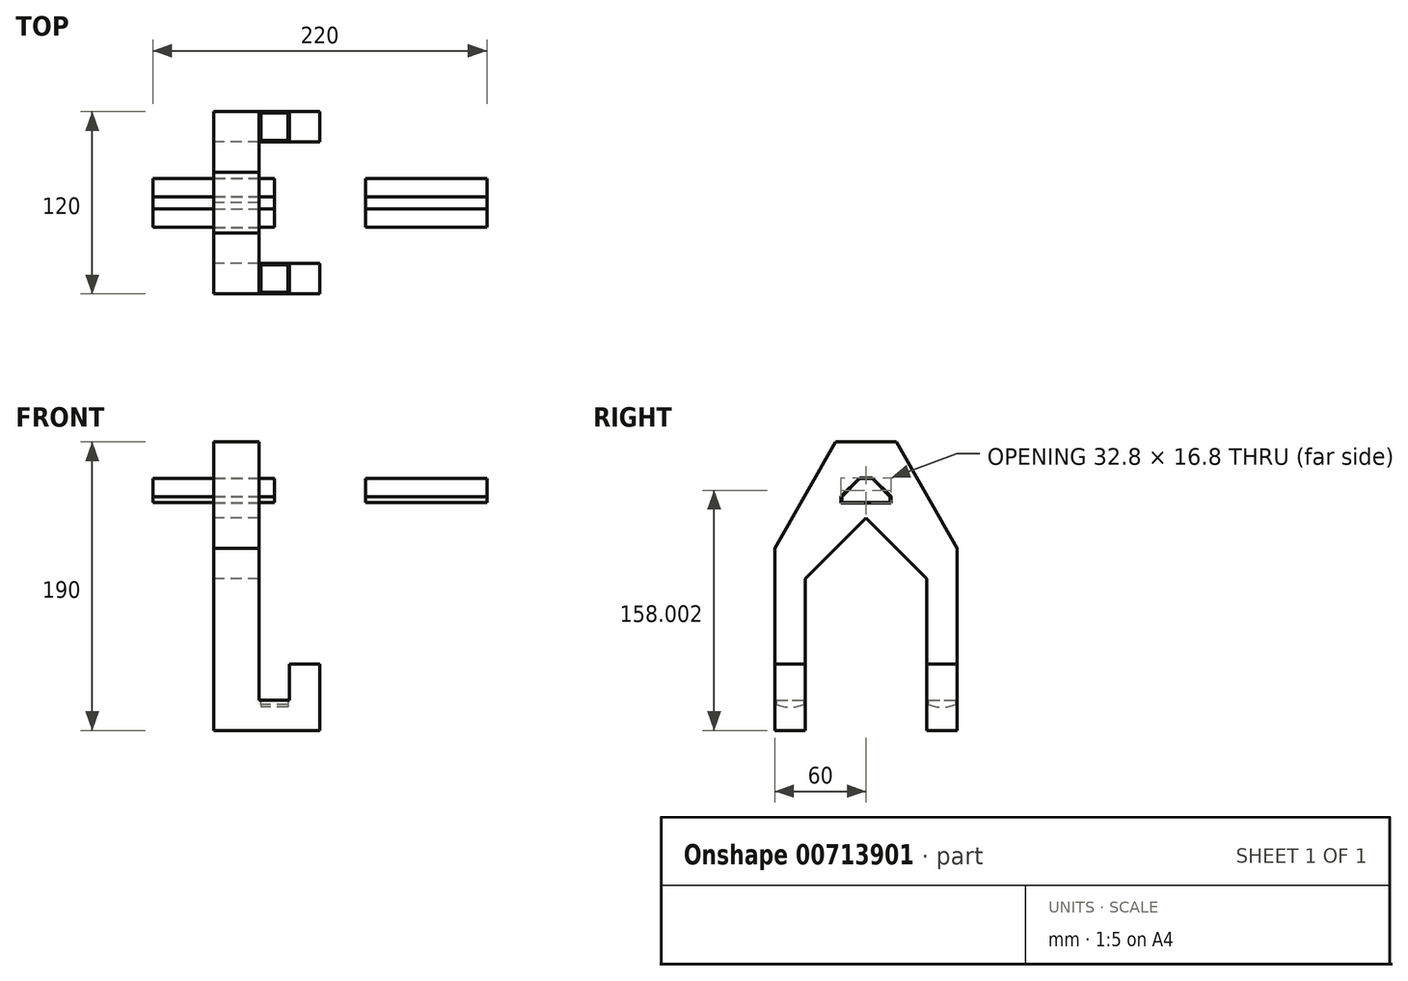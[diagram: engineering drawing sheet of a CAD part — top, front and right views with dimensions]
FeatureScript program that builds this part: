
annotation { "Feature Type Name" : "Feature", "Feature Type Description" : "" }
export const myFeature = defineFeature(function(context is Context, id is Id, definition is map)
    precondition{}
    {
        {
            var Q0;
            Q0=qCreatedBy(makeId("Front.planeOp"),FACE);
            var sketch = newSketch(context, id + "F0", { "sketchPlane" : qUnion([Q0])});
            skLineSegment(sketch, "E0", {"start": v(0, -71.5) * mm, "end": v(70, -71.5) * mm});
            skLineSegment(sketch, "E1", {"start": v(70, -71.5) * mm, "end": v(70, -27.82) * mm});
            skLineSegment(sketch, "E2", {"start": v(70, -27.82) * mm, "end": v(50, -27.82) * mm});
            skLineSegment(sketch, "E3", {"start": v(50, -27.82) * mm, "end": v(50, -51.5) * mm});
            skLineSegment(sketch, "E4", {"start": v(50, -51.5) * mm, "end": v(30, -51.5) * mm});
            skLineSegment(sketch, "E5", {"start": v(30, -51.5) * mm, "end": v(30, 0) * mm});
            skLineSegment(sketch, "E6", {"start": v(30, 0) * mm, "end": v(30, 118.5) * mm});
            skLineSegment(sketch, "E7", {"start": v(30, 118.5) * mm, "end": v(0, 118.5) * mm});
            skLineSegment(sketch, "E8", {"start": v(0, 118.5) * mm, "end": v(0, -71.5) * mm});
            skLineSegment(sketch, "E9", {"start": v(49, -51.5) * mm, "end": v(49, -54.5) * mm});
            skLineSegment(sketch, "E10", {"start": v(49, -54.5) * mm, "end": v(31, -54.5) * mm});
            skLineSegment(sketch, "E11", {"start": v(31, -54.5) * mm, "end": v(31, -51.5) * mm});
            skSolve(sketch);
        }
        {
            var Q0;
            Q0=makeQuery(id+"F0.imprint","IMPRINT",FACE,{"disambiguationData":[TD([[makeQuery(id+"F0.imprint","IMPRINT",EDGE,{"derivedFrom":sQuery(id+"F0.wireOp",EDGE,"E0")}),1.0]])]});
            var Q1;
            {var subQ0=sQuery(id+"F0.wireOp",EDGE,"E9");Q1=makeQuery(id+"F0.imprint","IMPRINT",FACE,{"disambiguationData":[TD([[makeQuery(id+"F0.imprint","IMPRINT",EDGE,{"derivedFrom":subQ0}),-1.0]])]});}
            extrude(context, id + "F1", {"entities" : qUnion([Q0, Q1]), "endBound" : BoundingType.SYMMETRIC, "depth" : 120 * mm, "offsetDistance" : 25 * mm, "hasSecondDirection" : true, "secondDirectionOppositeDirection" : true, "secondDirectionDepth" : 25 * mm});
        }
        {
            var Q0;
            Q0=makeQuery(id+"F1.opExtrude","SWEPT_FACE",FACE,{"disambiguationData":[OSD([sQuery(id+"F0.wireOp",EDGE,"E8")])]});
            var sketch = newSketch(context, id + "F2", { "sketchPlane" : qUnion([Q0])});
            skLineSegment(sketch, "E12.bottom", {"start": v(-40, -71.5) * mm, "end": v(40, -71.5) * mm});
            skLineSegment(sketch, "E12.top", {"start": v(-40, 28.5) * mm, "end": v(40, 28.5) * mm});
            skLineSegment(sketch, "E12.left", {"start": v(-40, -71.5) * mm, "end": v(-40, 28.5) * mm});
            skLineSegment(sketch, "E12.right", {"start": v(40, -71.5) * mm, "end": v(40, 28.5) * mm});
            skLineSegment(sketch, "E13", {"start": v(-40, 28.5) * mm, "end": v(0, 68.5) * mm});
            skLineSegment(sketch, "E14", {"start": v(0, 68.5) * mm, "end": v(40, 28.5) * mm});
            skSolve(sketch);
        }
        {
            var Q0;
            Q0=makeQuery(id+"F2.imprint","IMPRINT",FACE,{"disambiguationData":[TD([[makeQuery(id+"F2.imprint","IMPRINT",EDGE,{"derivedFrom":sQuery(id+"F2.wireOp",EDGE,"E12.bottom")}),-1.0]])]});
            var Q1;
            Q1=makeQuery(id+"F2.imprint","IMPRINT",FACE,{"disambiguationData":[TD([[makeQuery(id+"F2.imprint","IMPRINT",EDGE,{"derivedFrom":sQuery(id+"F2.wireOp",EDGE,"E12.top")}),1.0]])]});
            extrude(context, id + "F3", {"entities" : qUnion([Q0, Q1]), "operationType" : NewBodyOperationType.REMOVE, "endBound" : BoundingType.THROUGH_ALL, "oppositeDirection" : true, "depth" : 25 * mm, "offsetDistance" : 25 * mm});
        }
        {
            var Q0;
            Q0=makeQuery(id+"F1.opExtrude","SWEPT_FACE",FACE,{"disambiguationData":[OSD([sQuery(id+"F0.wireOp",EDGE,"E8")])]});
            var sketch = newSketch(context, id + "F4", { "sketchPlane" : qUnion([Q0])});
            skLineSegment(sketch, "E15", {"start": v(-60, 118.5) * mm, "end": v(-108, 118.5) * mm});
            skLineSegment(sketch, "E16", {"start": v(-108, 118.5) * mm, "end": v(-108, 68.5) * mm});
            skLineSegment(sketch, "E17", {"start": v(-108, 68.5) * mm, "end": v(-88, 68.5) * mm});
            skLineSegment(sketch, "E18", {"start": v(-88, 68.5) * mm, "end": v(-88, 96.5) * mm});
            skLineSegment(sketch, "E19", {"start": v(-86, 98.5) * mm, "end": v(-62, 98.5) * mm});
            skPoint(sketch, "E20", {"position": v(-84.6, 98.5) * mm});
            skPoint(sketch, "E21", {"position": v(-62.05, 98.5) * mm});
            skPoint(sketch, "E22.visualSharp", {"position": v(-88, 98.5) * mm});
            skArc(sketch, "E22.filletArc", {"start": v(-86, 98.5) * mm, "mid": v(-87.41, 97.9) * mm, "end": v(-88, 96.5) * mm});
            skLineSegment(sketch, "E23", {"start": v(-60, 96.5) * mm, "end": v(-60, 92.19) * mm});
            skPoint(sketch, "E24.visualSharp", {"position": v(-60, 98.5) * mm});
            skArc(sketch, "E24.filletArc", {"start": v(-60, 96.5) * mm, "mid": v(-60.59, 97.9) * mm, "end": v(-62, 98.5) * mm});
            skLineSegment(sketch, "E25", {"start": v(-60, 98.5) * mm, "end": v(-60, 13.5) * mm});
            skLineSegment(sketch, "E26", {"start": v(-60, 13.5) * mm, "end": v(-108.1, 13.5) * mm});
            skLineSegment(sketch, "E27", {"start": v(-108.1, 13.5) * mm, "end": v(-60, -34.62) * mm});
            skLineSegment(sketch, "E28", {"start": v(-60, 13.5) * mm, "end": v(-60, -34.62) * mm});
            skSolve(sketch);
        }
        {
            var Q0;
            {var subQ0=sQuery(id+"F0.wireOp",EDGE,"E8");Q0=makeQuery(id+"FtPaMowYWSEWgdu_1.boolean.opBoolean","MERGE",FACE,{"derivedFrom":[makeQuery(id+"F1.opExtrude","SWEPT_FACE",FACE,{"disambiguationData":[OSD([subQ0])]}),makeQuery(id+"FtPaMowYWSEWgdu_1.opExtrude","CAP_FACE",FACE,{"disambiguationData":[OSD([subQ0,sQuery(id+"F4.wireOp",EDGE,"E15"),sQuery(id+"F4.wireOp",EDGE,"E16"),sQuery(id+"F4.wireOp",EDGE,"E17"),sQuery(id+"F4.wireOp",EDGE,"E18"),sQuery(id+"F4.wireOp",EDGE,"E19"),sQuery(id+"F4.wireOp",EDGE,"E22.filletArc"),sQuery(id+"F4.wireOp",EDGE,"E24.filletArc")])],"isStart":true})]});}
            var sketch = newSketch(context, id + "F5", { "sketchPlane" : qUnion([Q0])});
            skLineSegment(sketch, "E29", {"start": v(-42.74, 118.5) * mm, "end": v(60, 118.5) * mm});
            skLineSegment(sketch, "E30", {"start": v(60, 118.5) * mm, "end": v(60, 41.85) * mm});
            skLineSegment(sketch, "E31", {"start": v(-40, 28.5) * mm, "end": v(40, 28.5) * mm});
            skLineSegment(sketch, "E32", {"start": v(-40, 118.5) * mm, "end": v(-40, 98.5) * mm});
            skLineSegment(sketch, "E33", {"start": v(-40, 98.5) * mm, "end": v(0, 98.5) * mm});
            skLineSegment(sketch, "E34", {"start": v(0, 98.5) * mm, "end": v(0, 78.5) * mm});
            skLineSegment(sketch, "E35", {"start": v(0, 78.5) * mm, "end": v(20, 78.5) * mm});
            skLineSegment(sketch, "E36", {"start": v(20, 78.5) * mm, "end": v(0, 98.5) * mm});
            skLineSegment(sketch, "E37", {"start": v(0, 98.5) * mm, "end": v(-20, 78.5) * mm});
            skLineSegment(sketch, "E38", {"start": v(-20, 78.5) * mm, "end": v(0, 78.5) * mm});
            skLineSegment(sketch, "E39", {"start": v(-20, 78.5) * mm, "end": v(-20, 118.5) * mm});
            skLineSegment(sketch, "E40", {"start": v(-20, 118.5) * mm, "end": v(-60, 48.5) * mm});
            skLineSegment(sketch, "E41", {"start": v(-60, 48.5) * mm, "end": v(-60, 28.5) * mm});
            skLineSegment(sketch, "E42", {"start": v(-60, 28.5) * mm, "end": v(-40, 28.5) * mm});
            skLineSegment(sketch, "E43", {"start": v(40, 28.5) * mm, "end": v(60, 28.5) * mm});
            skLineSegment(sketch, "E44", {"start": v(60, 28.5) * mm, "end": v(60, 48.5) * mm});
            skLineSegment(sketch, "E45", {"start": v(60, 48.5) * mm, "end": v(20, 118.5) * mm});
            skLineSegment(sketch, "E46", {"start": v(16, 82.5) * mm, "end": v(16, 78.5) * mm});
            skLineSegment(sketch, "E47", {"start": v(-16, 82.5) * mm, "end": v(-16, 78.5) * mm});
            skLineSegment(sketch, "E48", {"start": v(4, 94.5) * mm, "end": v(-4, 94.5) * mm});
            skSolve(sketch);
        }
        {
            var Q0;
            {var subQ0=sQuery(id+"F0.wireOp",EDGE,"E9");Q0=makeQuery(id+"F0.imprint","IMPRINT",FACE,{"disambiguationData":[TD([[makeQuery(id+"F0.imprint","IMPRINT",EDGE,{"derivedFrom":subQ0}),-1.0]])]});}
            extrude(context, id + "F6", {"entities" : qUnion([Q0]), "depth" : 18 * mm, "offsetDistance" : 25 * mm});
        }
        {
            var Q0;
            Q0=makeQuery(id+"F6.opExtrude","SWEPT_FACE",FACE,{"disambiguationData":[OSD([sQuery(id+"F0.wireOp",EDGE,"E11")])]});
            var sketch = newSketch(context, id + "F7", { "sketchPlane" : qUnion([Q0])});
            skArc(sketch, "E49", {"start": v(0, -54.5) * mm, "mid": v(9, -56.2) * mm, "end": v(18, -54.5) * mm});
            skSolve(sketch);
        }
        {
            var Q0;
            Q0 = qSketchRegion(id + "F7", true);
            var Q1;
            Q1=makeQuery(id+"F7.imprint","IMPRINT",FACE,{"disambiguationData":[TD([[makeQuery(id+"F7.imprint","IMPRINT",EDGE,{"derivedFrom":sQuery(id+"F7.wireOp",EDGE,"E49")}),1.0]])]});
            var Q2;
            Q2=makeQuery(id+"F6.opExtrude","CAP_VERTEX",VERTEX,{"disambiguationData":[OSD([sQuery(id+"F0.wireOp",EDGE,"E9"),sQuery(id+"F0.wireOp",EDGE,"E10")])],"isStart":false});
            extrude(context, id + "F8", {"entities" : qUnion([Q0, Q1]), "operationType" : NewBodyOperationType.ADD, "endBound" : BoundingType.UP_TO_VERTEX, "oppositeDirection" : true, "depth" : 25 * mm, "endBoundEntityVertex" : qUnion([Q2]), "offsetDistance" : 25 * mm});
        }
        {
            var Q0;
            Q0=makeQuery(id+"F6.opExtrude","SWEPT_BODY",BODY,{"disambiguationData":[OSD([sQuery(id+"F0.wireOp",EDGE,"E4"),sQuery(id+"F0.wireOp",EDGE,"E9"),sQuery(id+"F0.wireOp",EDGE,"E10"),sQuery(id+"F0.wireOp",EDGE,"E11")])]});
            transform(context, id + "F9", {"entities" : qUnion([Q0]), "transformType" : TransformType.TRANSLATION_3D, "dx" : 0 * mm, "dy" : -41 * mm, "dz" : 0 * mm, "makeCopy" : true});
        }
        {
            var Q0;
            Q0=makeQuery(id+"F6.opExtrude","SWEPT_BODY",BODY,{"disambiguationData":[OSD([sQuery(id+"F0.wireOp",EDGE,"E4"),sQuery(id+"F0.wireOp",EDGE,"E9"),sQuery(id+"F0.wireOp",EDGE,"E10"),sQuery(id+"F0.wireOp",EDGE,"E11")])]});
            transform(context, id + "F10", {"entities" : qUnion([Q0]), "transformType" : TransformType.TRANSLATION_3D, "dx" : 0 * mm, "dy" : 59 * mm, "dz" : 0 * mm, "makeCopy" : false});
        }
        {
            var Q0;
            Q0=makeQuery(id+"F9.opPattern","COPY",BODY,{"derivedFrom":makeQuery(id+"F6.opExtrude","SWEPT_BODY",BODY,{"disambiguationData":[OSD([sQuery(id+"F0.wireOp",EDGE,"E4"),sQuery(id+"F0.wireOp",EDGE,"E9"),sQuery(id+"F0.wireOp",EDGE,"E10"),sQuery(id+"F0.wireOp",EDGE,"E11")])]}),"instanceName":"1"});
            var Q1;
            Q1=makeQuery(id+"F6.opExtrude","SWEPT_BODY",BODY,{"disambiguationData":[OSD([sQuery(id+"F0.wireOp",EDGE,"E4"),sQuery(id+"F0.wireOp",EDGE,"E9"),sQuery(id+"F0.wireOp",EDGE,"E10"),sQuery(id+"F0.wireOp",EDGE,"E11")])]});
            var Q2;
            Q2=makeQuery(id+"F1.opExtrude","SWEPT_BODY",BODY,{"disambiguationData":[OSD([sQuery(id+"F0.wireOp",EDGE,"E0"),sQuery(id+"F0.wireOp",EDGE,"E1"),sQuery(id+"F0.wireOp",EDGE,"E2"),sQuery(id+"F0.wireOp",EDGE,"E3"),sQuery(id+"F0.wireOp",EDGE,"E4"),sQuery(id+"F0.wireOp",EDGE,"E5"),sQuery(id+"F0.wireOp",EDGE,"E6"),sQuery(id+"F0.wireOp",EDGE,"E7"),sQuery(id+"F0.wireOp",EDGE,"E8")])]});
            booleanBodies(context, id + "F11", {"operationType" : BooleanOperationType.SUBTRACTION, "tools" : qUnion([Q0, Q1]), "targets" : qUnion([Q2])});
        }
        {
            var Q0;
            {var subQ0=sQuery(id+"F5.wireOp",EDGE,"E47");Q0=makeQuery(id+"F5.imprint","IMPRINT",FACE,{"disambiguationData":[TD([[makeQuery(id+"F5.imprint","IMPRINT",EDGE,{"derivedFrom":subQ0}),1.0]])]});}
            var Q1;
            {var subQ0=sQuery(id+"F5.wireOp",EDGE,"E46");Q1=makeQuery(id+"F5.imprint","IMPRINT",FACE,{"disambiguationData":[TD([[makeQuery(id+"F5.imprint","IMPRINT",EDGE,{"derivedFrom":subQ0}),-1.0]])]});}
            extrude(context, id + "F12", {"entities" : qUnion([Q0, Q1]), "endBound" : BoundingType.SYMMETRIC, "depth" : 80 * mm, "offsetDistance" : 25 * mm});
        }
        {
            var Q0;
            {var subQ1=sQuery(id+"F5.wireOp",EDGE,"E32");Q0=makeQuery(id+"F5.imprint","IMPRINT",FACE,{"disambiguationData":[TD([[makeQuery(id+"F5.imprint","IMPRINT",EDGE,{"derivedFrom":subQ1}),-1.0]])]});}
            var Q1;
            {var subQ0=sQuery(id+"F5.wireOp",EDGE,"E32");Q1=makeQuery(id+"F5.imprint","IMPRINT",FACE,{"disambiguationData":[TD([[makeQuery(id+"F5.imprint","IMPRINT",EDGE,{"derivedFrom":subQ0}),1.0]])]});}
            var Q2;
            {var subQ0=sQuery(id+"F5.wireOp",EDGE,"E30");Q2=makeQuery(id+"F5.imprint","IMPRINT",FACE,{"disambiguationData":[TD([[makeQuery(id+"F5.imprint","IMPRINT",EDGE,{"derivedFrom":subQ0}),-1.0]])]});}
            extrude(context, id + "F13", {"entities" : qUnion([Q0, Q1, Q2]), "operationType" : NewBodyOperationType.REMOVE, "endBound" : BoundingType.THROUGH_ALL, "oppositeDirection" : true, "depth" : 25 * mm, "offsetDistance" : 25 * mm});
        }
        {
            var Q0;
            Q0=makeQuery(id+"F12.opExtrude","SWEPT_BODY",BODY,{"disambiguationData":[OSD([sQuery(id+"F5.wireOp",EDGE,"E35"),sQuery(id+"F5.wireOp",EDGE,"E36"),sQuery(id+"F5.wireOp",EDGE,"E37"),sQuery(id+"F5.wireOp",EDGE,"E38")])]});
            var Q1;
            Q1=makeQuery(id+"F1.opExtrude","SWEPT_BODY",BODY,{"disambiguationData":[OSD([sQuery(id+"F0.wireOp",EDGE,"E0"),sQuery(id+"F0.wireOp",EDGE,"E1"),sQuery(id+"F0.wireOp",EDGE,"E2"),sQuery(id+"F0.wireOp",EDGE,"E3"),sQuery(id+"F0.wireOp",EDGE,"E4"),sQuery(id+"F0.wireOp",EDGE,"E5"),sQuery(id+"F0.wireOp",EDGE,"E6"),sQuery(id+"F0.wireOp",EDGE,"E7"),sQuery(id+"F0.wireOp",EDGE,"E8")])]});
            booleanBodies(context, id + "F14", {"operationType" : BooleanOperationType.SUBTRACTION, "tools" : qUnion([Q0]), "targets" : qUnion([Q1]), "offset" : true, "offsetAll" : true, "offsetDistance" : 0.4 * mm, "keepTools" : true});
        }
        {
            var Q0;
            Q0=makeQuery(id+"F12.opExtrude","SWEPT_BODY",BODY,{"disambiguationData":[OSD([sQuery(id+"F5.wireOp",EDGE,"E35"),sQuery(id+"F5.wireOp",EDGE,"E36"),sQuery(id+"F5.wireOp",EDGE,"E37"),sQuery(id+"F5.wireOp",EDGE,"E38"),sQuery(id+"F5.wireOp",EDGE,"E46"),sQuery(id+"F5.wireOp",EDGE,"E47"),sQuery(id+"F5.wireOp",EDGE,"E48")])]});
            transform(context, id + "F15", {"entities" : qUnion([Q0]), "transformType" : TransformType.TRANSLATION_3D, "dx" : 140 * mm, "dy" : 0 * mm, "dz" : 0 * mm, "makeCopy" : true});
        }
    });
